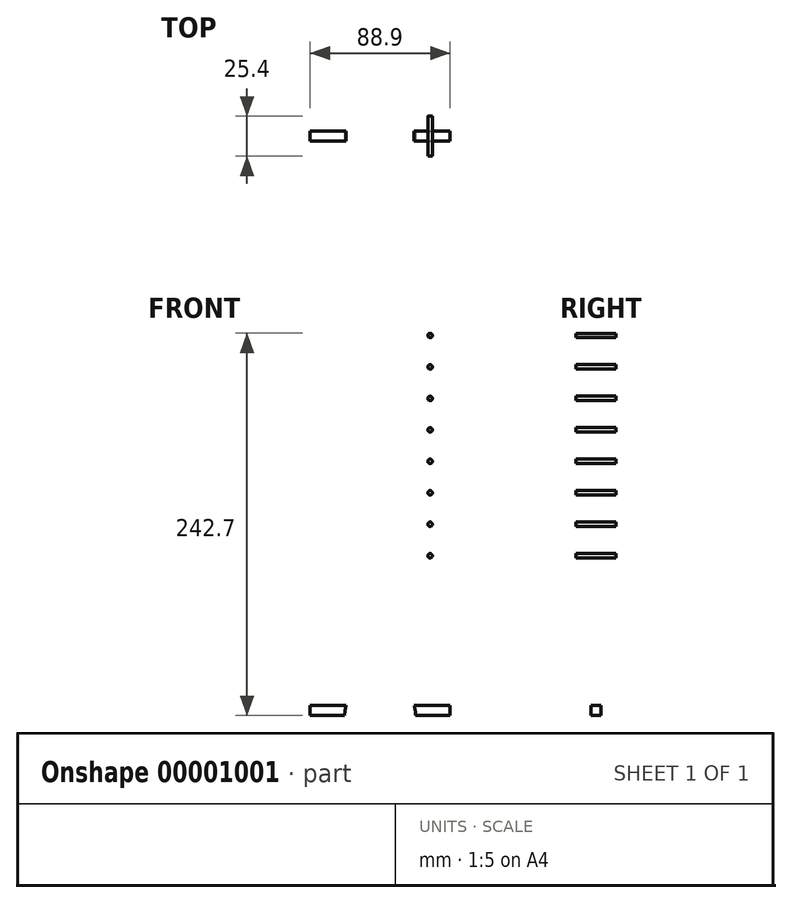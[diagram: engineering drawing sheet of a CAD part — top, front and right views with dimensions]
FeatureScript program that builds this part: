
annotation { "Feature Type Name" : "Feature", "Feature Type Description" : "" }
export const myFeature = defineFeature(function(context is Context, id is Id, definition is map)
    precondition{}
    {
        {
            var Q0;
            Q0=qCreatedBy(makeId("Top.planeOp"),FACE);
            var sketch = newSketch(context, id + "F0", { "sketchPlane" : qUnion([Q0])});
            skLineSegment(sketch, "E0.bottom", {"start": v(-44.45, 12.7) * mm, "end": v(44.45, 12.7) * mm});
            skLineSegment(sketch, "E0.top", {"start": v(-44.45, -12.7) * mm, "end": v(44.45, -12.7) * mm});
            skLineSegment(sketch, "E0.left", {"start": v(-44.45, 12.7) * mm, "end": v(-44.45, -12.7) * mm});
            skLineSegment(sketch, "E0.right", {"start": v(44.45, 12.7) * mm, "end": v(44.45, -12.7) * mm});
            skSolve(sketch);
        }
        {
            var Q0;
            Q0=makeQuery(id+"F0.imprint","IMPRINT",FACE,{"disambiguationData":[TD([[makeQuery(id+"F0.imprint","IMPRINT",EDGE,{"derivedFrom":sQuery(id+"F0.wireOp",EDGE,"E0.bottom")}),-1.0]])]});
            extrude(context, id + "F1", {"entities" : qUnion([Q0]), "endBound" : BoundingType.SYMMETRIC, "depth" : 254 * mm});
        }
        {
            var Q0;
            Q0=makeQuery(id+"F1.opExtrude","CAP_FACE",FACE,{"disambiguationData":[OSD([sQuery(id+"F0.wireOp",EDGE,"E0.bottom"),sQuery(id+"F0.wireOp",EDGE,"E0.top"),sQuery(id+"F0.wireOp",EDGE,"E0.left"),sQuery(id+"F0.wireOp",EDGE,"E0.right")])],"isStart":true});
            var sketch = newSketch(context, id + "F2", { "sketchPlane" : qUnion([Q0])});
            skCircle(sketch, "E1", {"center": v(-28.58, 7.94) * mm, "radius": 2.8 * mm});
            skCircle(sketch, "E2", {"center": v(-38.1, -7.94) * mm, "radius": 2.8 * mm});
            skCircle(sketch, "E3", {"center": v(28.58, 7.94) * mm, "radius": 2.8 * mm});
            skCircle(sketch, "E4", {"center": v(38.1, -7.94) * mm, "radius": 2.8 * mm});
            skCircle(sketch, "E5", {"center": v(-25.4, -7.94) * mm, "radius": 3.18 * mm});
            skCircle(sketch, "E6", {"center": v(25.4, -7.94) * mm, "radius": 3.18 * mm});
            skSolve(sketch);
        }
        {
            var Q0;
            {Q0=qUnion([makeQuery(id+"F2.imprint","IMPRINT",FACE,{"disambiguationData":[TD([[makeQuery(id+"F2.imprint","IMPRINT",EDGE,{"derivedFrom":sQuery(id+"F2.wireOp",EDGE,"E1")}),1.0]])]}),makeQuery(id+"F2.imprint","IMPRINT",FACE,{"disambiguationData":[TD([[makeQuery(id+"F2.imprint","IMPRINT",EDGE,{"derivedFrom":sQuery(id+"F2.wireOp",EDGE,"E2")}),1.0]])]}),makeQuery(id+"F2.imprint","IMPRINT",FACE,{"disambiguationData":[TD([[makeQuery(id+"F2.imprint","IMPRINT",EDGE,{"derivedFrom":sQuery(id+"F2.wireOp",EDGE,"E3")}),1.0]])]}),makeQuery(id+"F2.imprint","IMPRINT",FACE,{"disambiguationData":[TD([[makeQuery(id+"F2.imprint","IMPRINT",EDGE,{"derivedFrom":sQuery(id+"F2.wireOp",EDGE,"E4")}),1.0]])]}),makeQuery(id+"F2.imprint","IMPRINT",FACE,{"disambiguationData":[TD([[makeQuery(id+"F2.imprint","IMPRINT",EDGE,{"derivedFrom":sQuery(id+"F2.wireOp",EDGE,"E5")}),1.0]])]}),makeQuery(id+"F2.imprint","IMPRINT",FACE,{"disambiguationData":[TD([[makeQuery(id+"F2.imprint","IMPRINT",EDGE,{"derivedFrom":sQuery(id+"F2.wireOp",EDGE,"E6")}),1.0]])]})]);}
            extrude(context, id + "F3", {"entities" : qUnion([Q0]), "operationType" : NewBodyOperationType.REMOVE, "oppositeDirection" : true, "depth" : 25.4 * mm});
        }
        {
            var Q0;
            Q0=makeQuery(id+"F1.opExtrude","SWEPT_FACE",FACE,{"disambiguationData":[OSD([sQuery(id+"F0.wireOp",EDGE,"E0.top")])]});
            var sketch = newSketch(context, id + "F4", { "sketchPlane" : qUnion([Q0])});
            skCircle(sketch, "E7", {"center": v(0, -127) * mm, "radius": 22.5 * mm});
            skSolve(sketch);
        }
        {
            var Q0;
            {var subQ0=makeQuery(id+"F1.opExtrude","CAP_EDGE",EDGE,{"disambiguationData":[OSD([sQuery(id+"F0.wireOp",EDGE,"E0.top")])],"isStart":true});var subQ1=sQuery(id+"F4.wireOp",EDGE,"E7");var subQ3=makeQuery(id+"F4.imprint","INTERSECT",VERTEX,{"disambiguationData":[OD(0.0)],"derivedFrom":[subQ0,subQ1]});Q0=qUnion([makeQuery(id+"F4.imprint","IMPRINT",FACE,{"disambiguationData":[TD([[makeQuery(id+"F4.imprint","IMPRINT",EDGE,{"disambiguationData":[TD([[subQ3,-1.0]])],"derivedFrom":subQ1}),1.0]])]}),makeQuery(id+"F4.imprint","IMPRINT",FACE,{"disambiguationData":[TD([[makeQuery(id+"F4.imprint","IMPRINT",EDGE,{"disambiguationData":[TD([[subQ3,1.0]])],"derivedFrom":subQ1}),1.0]])]})]);}
            extrude(context, id + "F5", {"entities" : qUnion([Q0]), "operationType" : NewBodyOperationType.REMOVE, "oppositeDirection" : true, "depth" : 25.4 * mm});
        }
        {
            var Q0;
            {var subQ0=sQuery(id+"F0.wireOp",EDGE,"E0.bottom");var subQ1=sQuery(id+"F0.wireOp",EDGE,"E0.top");var subQ2=sQuery(id+"F0.wireOp",EDGE,"E0.left");Q0=makeQuery(id+"F5.boolean.opBoolean","SPLIT",FACE,{"disambiguationData":[TD([makeQuery(id+"F1.opExtrude","SWEPT_FACE",FACE,{"disambiguationData":[OSD([subQ2])]})])],"derivedFrom":makeQuery(id+"F1.opExtrude","CAP_FACE",FACE,{"disambiguationData":[OSD([subQ0,subQ1,subQ2,sQuery(id+"F0.wireOp",EDGE,"E0.right")])],"isStart":true})});}
            var sketch = newSketch(context, id + "F6", { "sketchPlane" : qUnion([Q0])});
            skLineSegment(sketch, "E8.bottom", {"start": v(-44.45, 3.18) * mm, "end": v(44.45, 3.18) * mm});
            skLineSegment(sketch, "E8.top", {"start": v(-44.45, -3.18) * mm, "end": v(44.45, -3.18) * mm});
            skLineSegment(sketch, "E9.bottom", {"start": v(-44.45, 12.7) * mm, "end": v(44.45, 12.7) * mm});
            skLineSegment(sketch, "E9.top", {"start": v(-44.45, -12.7) * mm, "end": v(44.45, -12.7) * mm});
            skLineSegment(sketch, "E9.left", {"start": v(-44.45, 12.7) * mm, "end": v(-44.45, 3.18) * mm});
            skLineSegment(sketch, "E9.right", {"start": v(44.45, 12.7) * mm, "end": v(44.45, 3.18) * mm});
            skLineSegment(sketch, "E10.trimOffspring", {"start": v(-44.45, -3.18) * mm, "end": v(-44.45, -12.7) * mm});
            skLineSegment(sketch, "E11.trimOffspring", {"start": v(44.45, -3.18) * mm, "end": v(44.45, -12.7) * mm});
            skSolve(sketch);
        }
        {
            var Q0;
            Q0=makeQuery(id+"F6.imprint","IMPRINT",FACE,{"disambiguationData":[TD([[makeQuery(id+"F6.imprint","IMPRINT",EDGE,{"derivedFrom":makeQuery(id+"F3.boolean.opBoolean","COPY",EDGE,{"derivedFrom":makeQuery(id+"F3.opExtrude","CAP_EDGE",EDGE,{"disambiguationData":[OSD([sQuery(id+"F2.wireOp",EDGE,"E1")])],"isStart":true})})}),1.0]])]});
            var Q1;
            Q1=makeQuery(id+"F6.imprint","IMPRINT",FACE,{"disambiguationData":[TD([[makeQuery(id+"F6.imprint","IMPRINT",EDGE,{"derivedFrom":makeQuery(id+"F3.boolean.opBoolean","COPY",EDGE,{"derivedFrom":makeQuery(id+"F3.opExtrude","CAP_EDGE",EDGE,{"disambiguationData":[OSD([sQuery(id+"F2.wireOp",EDGE,"E2")])],"isStart":true})})}),1.0]])]});
            var Q2;
            {var subQ7=sQuery(id+"F6.wireOp",EDGE,"E11.trimOffspring");Q2=makeQuery(id+"F6.imprint","IMPRINT",FACE,{"disambiguationData":[TD([[makeQuery(id+"F6.imprint","IMPRINT",EDGE,{"derivedFrom":subQ7}),-1.0]])]});}
            var Q3;
            {var subQ5=sQuery(id+"F6.wireOp",EDGE,"E9.right");Q3=makeQuery(id+"F6.imprint","IMPRINT",FACE,{"disambiguationData":[TD([[makeQuery(id+"F6.imprint","IMPRINT",EDGE,{"derivedFrom":subQ5}),-1.0]])]});}
            var Q4;
            {var subQ7=sQuery(id+"F6.wireOp",EDGE,"E11.trimOffspring");Q4=makeQuery(id+"F6.imprint","IMPRINT",FACE,{"disambiguationData":[TD([[makeQuery(id+"F6.imprint","IMPRINT",EDGE,{"derivedFrom":subQ7}),-1.0]])]});}
            var Q5;
            {var subQ5=sQuery(id+"F6.wireOp",EDGE,"E8.left");Q5=makeQuery(id+"F6.imprint","IMPRINT",FACE,{"disambiguationData":[TD([[makeQuery(id+"F6.imprint","IMPRINT",EDGE,{"derivedFrom":subQ5}),-1.0]])]});}
            var Q6;
            {var subQ6=sQuery(id+"F6.wireOp",EDGE,"E9.left");Q6=makeQuery(id+"F6.imprint","IMPRINT",FACE,{"disambiguationData":[TD([[makeQuery(id+"F6.imprint","IMPRINT",EDGE,{"derivedFrom":subQ6}),-1.0]])]});}
            var Q7;
            {var subQ5=sQuery(id+"F6.wireOp",EDGE,"E8.right");Q7=makeQuery(id+"F6.imprint","IMPRINT",FACE,{"disambiguationData":[TD([[makeQuery(id+"F6.imprint","IMPRINT",EDGE,{"derivedFrom":subQ5}),-1.0]])]});}
            var Q8;
            {var subQ8=sQuery(id+"F6.wireOp",EDGE,"E10.trimOffspring");Q8=makeQuery(id+"F6.imprint","IMPRINT",FACE,{"disambiguationData":[TD([[makeQuery(id+"F6.imprint","IMPRINT",EDGE,{"derivedFrom":subQ8}),-1.0]])]});}
            extrude(context, id + "F7", {"entities" : qUnion([Q0, Q1, Q2, Q3, Q4, Q5, Q6, Q7, Q8]), "operationType" : NewBodyOperationType.REMOVE, "oppositeDirection" : true, "depth" : 6.35 * mm});
        }
        {
            var Q0;
            Q0=makeQuery(id+"F1.opExtrude","SWEPT_FACE",FACE,{"disambiguationData":[OSD([sQuery(id+"F0.wireOp",EDGE,"E0.top")])]});
            var sketch = newSketch(context, id + "F8", { "sketchPlane" : qUnion([Q0])});
            skCircle(sketch, "E12", {"center": v(-31.75, 114.3) * mm, "radius": 1.4 * mm});
            skCircle(sketch, "E13", {"center": v(-31.75, 94.3) * mm, "radius": 1.4 * mm});
            skCircle(sketch, "E14", {"center": v(-31.75, 74.3) * mm, "radius": 1.4 * mm});
            skCircle(sketch, "E15", {"center": v(-31.75, 54.31) * mm, "radius": 1.4 * mm});
            skCircle(sketch, "E16", {"center": v(-31.75, 34.32) * mm, "radius": 1.4 * mm});
            skCircle(sketch, "E17", {"center": v(-31.75, -25.65) * mm, "radius": 1.4 * mm});
            skCircle(sketch, "E18", {"center": v(-31.75, 14.33) * mm, "radius": 1.4 * mm});
            skCircle(sketch, "E19", {"center": v(-31.75, -5.66) * mm, "radius": 1.4 * mm});
            skLineSegment(sketch, "E20", {"start": v(0, 0) * mm, "end": v(0, 81.28) * mm, "construction": true});
            skCircle(sketch, "E21.0.MirrorC", {"center": v(31.75, 114.3) * mm, "radius": 1.4 * mm});
            skCircle(sketch, "E22.0.MirrorC", {"center": v(31.75, -25.65) * mm, "radius": 1.4 * mm});
            skCircle(sketch, "E22.2.MirrorC", {"center": v(31.75, 34.32) * mm, "radius": 1.4 * mm});
            skCircle(sketch, "E22.3.MirrorC", {"center": v(31.75, 54.31) * mm, "radius": 1.4 * mm});
            skCircle(sketch, "E22.4.MirrorC", {"center": v(31.75, 74.3) * mm, "radius": 1.4 * mm});
            skCircle(sketch, "E22.5.MirrorC", {"center": v(31.75, 14.33) * mm, "radius": 1.4 * mm});
            skCircle(sketch, "E22.6.MirrorC", {"center": v(31.75, -5.66) * mm, "radius": 1.4 * mm});
            skCircle(sketch, "E22.7.MirrorC", {"center": v(31.75, 94.3) * mm, "radius": 1.4 * mm});
            skSolve(sketch);
        }
        {
            var Q0;
            {Q0=qUnion([makeQuery(id+"F8.imprint","IMPRINT",FACE,{"disambiguationData":[TD([[makeQuery(id+"F8.imprint","IMPRINT",EDGE,{"derivedFrom":sQuery(id+"F8.wireOp",EDGE,"E12")}),1.0]])]}),makeQuery(id+"F8.imprint","IMPRINT",FACE,{"disambiguationData":[TD([[makeQuery(id+"F8.imprint","IMPRINT",EDGE,{"derivedFrom":sQuery(id+"F8.wireOp",EDGE,"E13")}),1.0]])]}),makeQuery(id+"F8.imprint","IMPRINT",FACE,{"disambiguationData":[TD([[makeQuery(id+"F8.imprint","IMPRINT",EDGE,{"derivedFrom":sQuery(id+"F8.wireOp",EDGE,"E14")}),1.0]])]}),makeQuery(id+"F8.imprint","IMPRINT",FACE,{"disambiguationData":[TD([[makeQuery(id+"F8.imprint","IMPRINT",EDGE,{"derivedFrom":sQuery(id+"F8.wireOp",EDGE,"E15")}),1.0]])]}),makeQuery(id+"F8.imprint","IMPRINT",FACE,{"disambiguationData":[TD([[makeQuery(id+"F8.imprint","IMPRINT",EDGE,{"derivedFrom":sQuery(id+"F8.wireOp",EDGE,"E16")}),1.0]])]}),makeQuery(id+"F8.imprint","IMPRINT",FACE,{"disambiguationData":[TD([[makeQuery(id+"F8.imprint","IMPRINT",EDGE,{"derivedFrom":sQuery(id+"F8.wireOp",EDGE,"E17")}),1.0]])]}),makeQuery(id+"F8.imprint","IMPRINT",FACE,{"disambiguationData":[TD([[makeQuery(id+"F8.imprint","IMPRINT",EDGE,{"derivedFrom":sQuery(id+"F8.wireOp",EDGE,"E18")}),1.0]])]}),makeQuery(id+"F8.imprint","IMPRINT",FACE,{"disambiguationData":[TD([[makeQuery(id+"F8.imprint","IMPRINT",EDGE,{"derivedFrom":sQuery(id+"F8.wireOp",EDGE,"E19")}),1.0]])]}),makeQuery(id+"F8.imprint","IMPRINT",FACE,{"disambiguationData":[TD([[makeQuery(id+"F8.imprint","IMPRINT",EDGE,{"derivedFrom":sQuery(id+"F8.wireOp",EDGE,"E22.0.MirrorC")}),-1.0]])]}),makeQuery(id+"F8.imprint","IMPRINT",FACE,{"disambiguationData":[TD([[makeQuery(id+"F8.imprint","IMPRINT",EDGE,{"derivedFrom":sQuery(id+"F8.wireOp",EDGE,"E21.0.MirrorC")}),-1.0]])]}),makeQuery(id+"F8.imprint","IMPRINT",FACE,{"disambiguationData":[TD([[makeQuery(id+"F8.imprint","IMPRINT",EDGE,{"derivedFrom":sQuery(id+"F8.wireOp",EDGE,"E22.2.MirrorC")}),-1.0]])]}),makeQuery(id+"F8.imprint","IMPRINT",FACE,{"disambiguationData":[TD([[makeQuery(id+"F8.imprint","IMPRINT",EDGE,{"derivedFrom":sQuery(id+"F8.wireOp",EDGE,"E22.3.MirrorC")}),-1.0]])]}),makeQuery(id+"F8.imprint","IMPRINT",FACE,{"disambiguationData":[TD([[makeQuery(id+"F8.imprint","IMPRINT",EDGE,{"derivedFrom":sQuery(id+"F8.wireOp",EDGE,"E22.4.MirrorC")}),-1.0]])]}),makeQuery(id+"F8.imprint","IMPRINT",FACE,{"disambiguationData":[TD([[makeQuery(id+"F8.imprint","IMPRINT",EDGE,{"derivedFrom":sQuery(id+"F8.wireOp",EDGE,"E22.5.MirrorC")}),-1.0]])]}),makeQuery(id+"F8.imprint","IMPRINT",FACE,{"disambiguationData":[TD([[makeQuery(id+"F8.imprint","IMPRINT",EDGE,{"derivedFrom":sQuery(id+"F8.wireOp",EDGE,"E22.6.MirrorC")}),-1.0]])]}),makeQuery(id+"F8.imprint","IMPRINT",FACE,{"disambiguationData":[TD([[makeQuery(id+"F8.imprint","IMPRINT",EDGE,{"derivedFrom":sQuery(id+"F8.wireOp",EDGE,"E22.7.MirrorC")}),-1.0]])]})]);}
            extrude(context, id + "F9", {"entities" : qUnion([Q0]), "operationType" : NewBodyOperationType.REMOVE, "endBound" : BoundingType.THROUGH_ALL, "oppositeDirection" : true, "depth" : 25.4 * mm});
        }
    });
